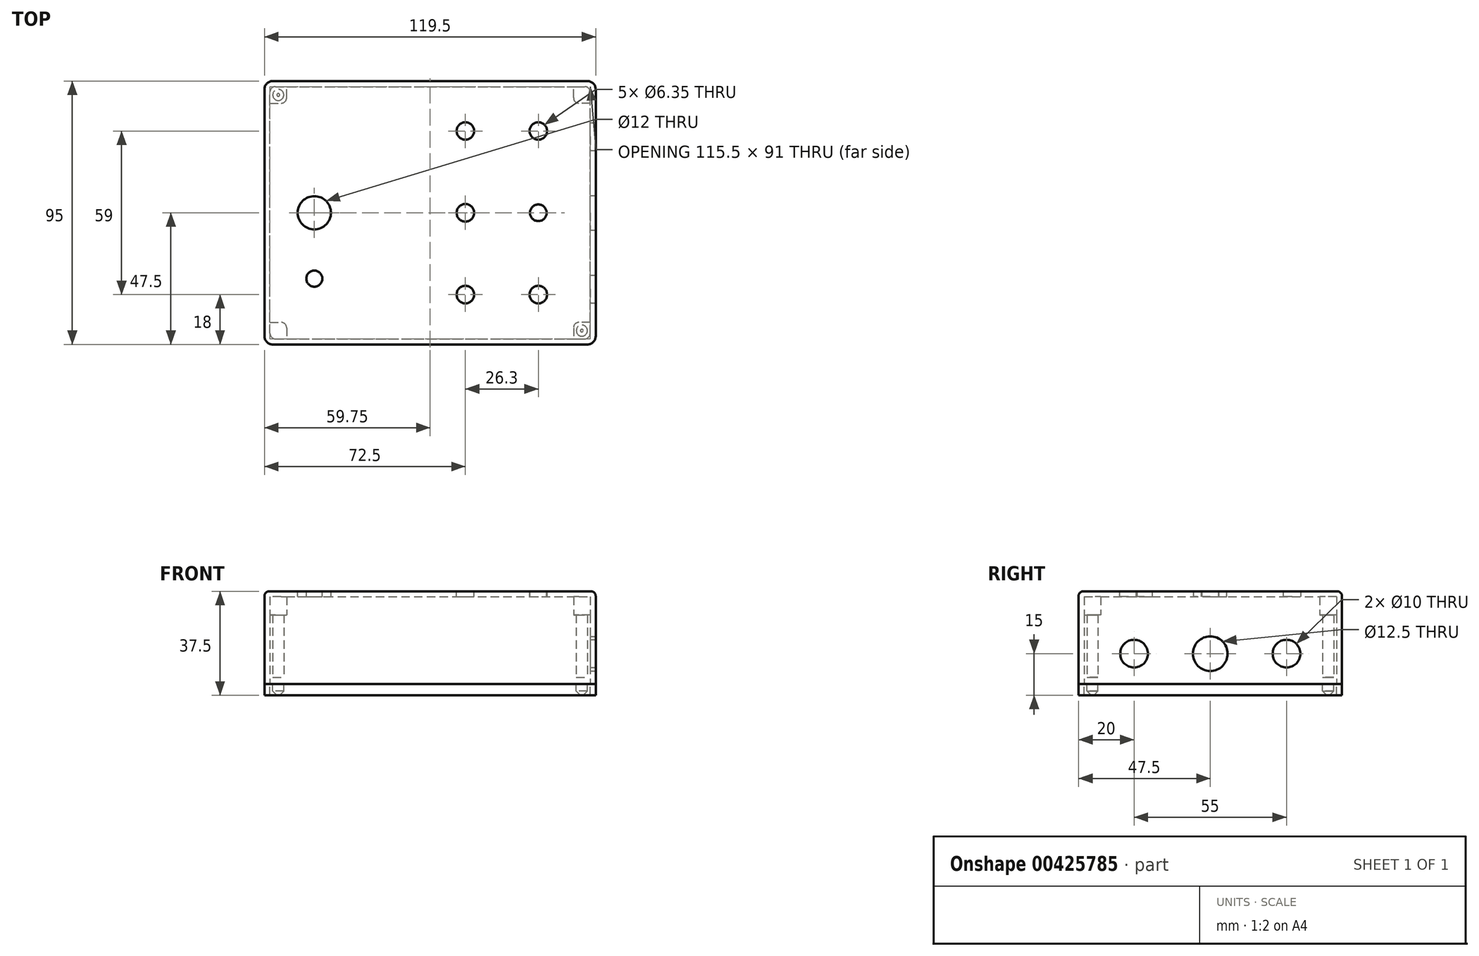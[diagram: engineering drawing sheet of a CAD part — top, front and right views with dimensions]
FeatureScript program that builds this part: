
annotation { "Feature Type Name" : "Feature", "Feature Type Description" : "" }
export const myFeature = defineFeature(function(context is Context, id is Id, definition is map)
    precondition{}
    {
        {
            var Q0;
            Q0=qCreatedBy(makeId("Top.planeOp"),FACE);
            var sketch = newSketch(context, id + "F0", { "sketchPlane" : qUnion([Q0])});
            skLineSegment(sketch, "E0.bottom", {"start": v(3, 0) * mm, "end": v(116.5, 0) * mm});
            skLineSegment(sketch, "E0.top", {"start": v(3, 95) * mm, "end": v(116.5, 95) * mm});
            skLineSegment(sketch, "E0.left", {"start": v(0, 3) * mm, "end": v(0, 92) * mm});
            skLineSegment(sketch, "E0.right", {"start": v(119.5, 3) * mm, "end": v(119.5, 92) * mm});
            skPoint(sketch, "E1.visualSharp", {"position": v(119.5, 95) * mm});
            skArc(sketch, "E1.filletArc", {"start": v(119.5, 92) * mm, "mid": v(118.62, 94.12) * mm, "end": v(116.5, 95) * mm});
            skPoint(sketch, "E2.visualSharp", {"position": v(119.5, 0) * mm});
            skArc(sketch, "E2.filletArc", {"start": v(116.5, 0) * mm, "mid": v(118.62, 0.88) * mm, "end": v(119.5, 3) * mm});
            skPoint(sketch, "E3.visualSharp", {"position": v(0, 0) * mm});
            skArc(sketch, "E3.filletArc", {"start": v(0, 3) * mm, "mid": v(0.88, 0.88) * mm, "end": v(3, 0) * mm});
            skPoint(sketch, "E4.visualSharp", {"position": v(0, 95) * mm});
            skArc(sketch, "E4.filletArc", {"start": v(3, 95) * mm, "mid": v(0.88, 94.12) * mm, "end": v(0, 92) * mm});
            skSolve(sketch);
        }
        {
            var Q0;
            Q0 = qSketchRegion(id + "F0", true);
            extrude(context, id + "F1", {"entities" : qUnion([Q0]), "depth" : 33.5 * mm});
        }
        {
            var Q0;
            Q0=makeQuery(id+"F1.opExtrude","CAP_FACE",FACE,{"disambiguationData":[OSD([sQuery(id+"F0.wireOp",EDGE,"E0.bottom"),sQuery(id+"F0.wireOp",EDGE,"E0.top"),sQuery(id+"F0.wireOp",EDGE,"E0.left"),sQuery(id+"F0.wireOp",EDGE,"E0.right"),sQuery(id+"F0.wireOp",EDGE,"E1.filletArc"),sQuery(id+"F0.wireOp",EDGE,"E2.filletArc"),sQuery(id+"F0.wireOp",EDGE,"E3.filletArc"),sQuery(id+"F0.wireOp",EDGE,"E4.filletArc")])],"isStart":true});
            var sketch = newSketch(context, id + "F2", { "sketchPlane" : qUnion([Q0])});
            skLineSegment(sketch, "E5.0", {"start": v(4.5, -2) * mm, "end": v(115, -2) * mm});
            skLineSegment(sketch, "E5.1", {"start": v(2, -4.5) * mm, "end": v(2, -90.5) * mm});
            skLineSegment(sketch, "E5.2", {"start": v(4.5, -93) * mm, "end": v(115, -93) * mm});
            skLineSegment(sketch, "E5.3", {"start": v(117.5, -4.5) * mm, "end": v(117.5, -90.5) * mm});
            skPoint(sketch, "E6.visualSharp", {"position": v(2, -2) * mm});
            skArc(sketch, "E6.filletArc", {"start": v(4.5, -2) * mm, "mid": v(2.73, -2.73) * mm, "end": v(2, -4.5) * mm});
            skPoint(sketch, "E7.visualSharp", {"position": v(117.5, -2) * mm});
            skArc(sketch, "E7.filletArc", {"start": v(117.5, -4.5) * mm, "mid": v(116.77, -2.73) * mm, "end": v(115, -2) * mm});
            skPoint(sketch, "E8.visualSharp", {"position": v(117.5, -93) * mm});
            skArc(sketch, "E8.filletArc", {"start": v(115, -93) * mm, "mid": v(116.77, -92.27) * mm, "end": v(117.5, -90.5) * mm});
            skPoint(sketch, "E9.visualSharp", {"position": v(2, -93) * mm});
            skArc(sketch, "E9.filletArc", {"start": v(2, -90.5) * mm, "mid": v(2.73, -92.27) * mm, "end": v(4.5, -93) * mm});
            skLineSegment(sketch, "E10", {"start": v(8, -2) * mm, "end": v(8, -6) * mm});
            skLineSegment(sketch, "E11", {"start": v(6, -8) * mm, "end": v(2, -8) * mm});
            skPoint(sketch, "E12.visualSharp", {"position": v(8, -8) * mm});
            skArc(sketch, "E12.filletArc", {"start": v(6, -8) * mm, "mid": v(7.41, -7.41) * mm, "end": v(8, -6) * mm});
            skLineSegment(sketch, "E13", {"start": v(59.75, 0) * mm, "end": v(59.75, -95) * mm, "construction": true});
            skLineSegment(sketch, "E14", {"start": v(0, -47.5) * mm, "end": v(119.5, -47.5) * mm, "construction": true});
            skLineSegment(sketch, "E15.MirrorCS", {"start": v(111.5, -2) * mm, "end": v(111.5, -6) * mm});
            skPoint(sketch, "E16.MirrorP", {"position": v(111.5, -8) * mm});
            skArc(sketch, "E17.MirrorCS", {"start": v(113.5, -8) * mm, "mid": v(112.09, -7.41) * mm, "end": v(111.5, -6) * mm});
            skLineSegment(sketch, "E18.MirrorCS", {"start": v(113.5, -8) * mm, "end": v(117.5, -8) * mm});
            skLineSegment(sketch, "E19.MirrorCS", {"start": v(6, -87) * mm, "end": v(2, -87) * mm});
            skArc(sketch, "E20.MirrorCS", {"start": v(6, -87) * mm, "mid": v(7.41, -87.59) * mm, "end": v(8, -89) * mm});
            skLineSegment(sketch, "E21.MirrorCS", {"start": v(8, -93) * mm, "end": v(8, -89) * mm});
            skLineSegment(sketch, "E22.MirrorCS", {"start": v(113.5, -87) * mm, "end": v(117.5, -87) * mm});
            skArc(sketch, "E23.MirrorCS", {"start": v(113.5, -87) * mm, "mid": v(112.09, -87.59) * mm, "end": v(111.5, -89) * mm});
            skLineSegment(sketch, "E24.MirrorCS", {"start": v(111.5, -93) * mm, "end": v(111.5, -89) * mm});
            skSolve(sketch);
        }
        {
            var Q0;
            {var subQ2=sQuery(id+"F2.wireOp",EDGE,"E10");Q0=makeQuery(id+"F2.imprint","IMPRINT",FACE,{"disambiguationData":[TD([[makeQuery(id+"F2.imprint","IMPRINT",EDGE,{"derivedFrom":subQ2}),1.0]])]});}
            extrude(context, id + "F3", {"entities" : qUnion([Q0]), "operationType" : NewBodyOperationType.REMOVE, "oppositeDirection" : true, "depth" : 31.5 * mm});
        }
        {
            var Q0;
            Q0=makeQuery(id+"F1.opExtrude","CAP_FACE",FACE,{"disambiguationData":[OSD([sQuery(id+"F0.wireOp",EDGE,"E0.bottom"),sQuery(id+"F0.wireOp",EDGE,"E0.top"),sQuery(id+"F0.wireOp",EDGE,"E0.left"),sQuery(id+"F0.wireOp",EDGE,"E0.right"),sQuery(id+"F0.wireOp",EDGE,"E1.filletArc"),sQuery(id+"F0.wireOp",EDGE,"E2.filletArc"),sQuery(id+"F0.wireOp",EDGE,"E3.filletArc"),sQuery(id+"F0.wireOp",EDGE,"E4.filletArc")])],"isStart":true});
            var sketch = newSketch(context, id + "F4", { "sketchPlane" : qUnion([Q0])});
            skLineSegment(sketch, "E25", {"start": v(8, -2) * mm, "end": v(4, -2) * mm});
            skLineSegment(sketch, "E26", {"start": v(2, -4) * mm, "end": v(2, -8) * mm});
            skLineSegment(sketch, "E27", {"start": v(111.5, -2) * mm, "end": v(115.5, -2) * mm});
            skLineSegment(sketch, "E28", {"start": v(117.5, -4) * mm, "end": v(117.5, -8) * mm});
            skLineSegment(sketch, "E29", {"start": v(117.5, -87) * mm, "end": v(117.5, -91) * mm});
            skLineSegment(sketch, "E30", {"start": v(115.5, -93) * mm, "end": v(111.5, -93) * mm});
            skLineSegment(sketch, "E31", {"start": v(8, -93) * mm, "end": v(4, -93) * mm});
            skLineSegment(sketch, "E32", {"start": v(2, -91) * mm, "end": v(2, -87) * mm});
            skPoint(sketch, "E33.visualSharp", {"position": v(2, -2) * mm});
            skArc(sketch, "E33.filletArc", {"start": v(4, -2) * mm, "mid": v(2.59, -2.59) * mm, "end": v(2, -4) * mm});
            skPoint(sketch, "E34.visualSharp", {"position": v(117.5, -2) * mm});
            skArc(sketch, "E34.filletArc", {"start": v(117.5, -4) * mm, "mid": v(116.91, -2.59) * mm, "end": v(115.5, -2) * mm});
            skPoint(sketch, "E35.visualSharp", {"position": v(117.5, -93) * mm});
            skArc(sketch, "E35.filletArc", {"start": v(115.5, -93) * mm, "mid": v(116.91, -92.41) * mm, "end": v(117.5, -91) * mm});
            skPoint(sketch, "E36.visualSharp", {"position": v(2, -93) * mm});
            skArc(sketch, "E36.filletArc", {"start": v(2, -91) * mm, "mid": v(2.59, -92.41) * mm, "end": v(4, -93) * mm});
            skSolve(sketch);
        }
        {
            var Q0;
            Q0=makeQuery(id+"F4.imprint","IMPRINT",FACE,{"disambiguationData":[TD([[makeQuery(id+"F4.imprint","IMPRINT",EDGE,{"derivedFrom":sQuery(id+"F4.wireOp",EDGE,"E25")}),1.0]])]});
            var Q1;
            Q1=makeQuery(id+"F4.imprint","IMPRINT",FACE,{"disambiguationData":[TD([[makeQuery(id+"F4.imprint","IMPRINT",EDGE,{"derivedFrom":sQuery(id+"F4.wireOp",EDGE,"E27")}),-1.0]])]});
            var Q2;
            Q2=makeQuery(id+"F4.imprint","IMPRINT",FACE,{"disambiguationData":[TD([[makeQuery(id+"F4.imprint","IMPRINT",EDGE,{"derivedFrom":sQuery(id+"F4.wireOp",EDGE,"E29")}),-1.0]])]});
            var Q3;
            Q3=makeQuery(id+"F4.imprint","IMPRINT",FACE,{"disambiguationData":[TD([[makeQuery(id+"F4.imprint","IMPRINT",EDGE,{"derivedFrom":sQuery(id+"F4.wireOp",EDGE,"E31")}),-1.0]])]});
            extrude(context, id + "F5", {"entities" : qUnion([Q0, Q1, Q2, Q3]), "operationType" : NewBodyOperationType.REMOVE, "oppositeDirection" : true, "depth" : 2.5 * mm});
        }
        {
            var Q0;
            Q0=makeQuery(id+"F1.opExtrude","CAP_FACE",FACE,{"disambiguationData":[OSD([sQuery(id+"F0.wireOp",EDGE,"E0.bottom"),sQuery(id+"F0.wireOp",EDGE,"E0.top"),sQuery(id+"F0.wireOp",EDGE,"E0.left"),sQuery(id+"F0.wireOp",EDGE,"E0.right"),sQuery(id+"F0.wireOp",EDGE,"E1.filletArc"),sQuery(id+"F0.wireOp",EDGE,"E2.filletArc"),sQuery(id+"F0.wireOp",EDGE,"E3.filletArc"),sQuery(id+"F0.wireOp",EDGE,"E4.filletArc")])],"isStart":true});
            var sketch = newSketch(context, id + "F6", { "sketchPlane" : qUnion([Q0])});
            skCircle(sketch, "E37", {"center": v(5, -5) * mm, "radius": 2 * mm});
            skLineSegment(sketch, "E38", {"start": v(59.75, 0) * mm, "end": v(59.75, -95) * mm, "construction": true});
            skLineSegment(sketch, "E39", {"start": v(119.5, -47.5) * mm, "end": v(0, -47.5) * mm, "construction": true});
            skCircle(sketch, "E40.MirrorC", {"center": v(114.5, -5) * mm, "radius": 2 * mm});
            skLineSegment(sketch, "E41.MirrorCS", {"start": v(0, -47.5) * mm, "end": v(119.5, -47.5) * mm, "construction": true});
            skCircle(sketch, "E42.MirrorC", {"center": v(5, -90) * mm, "radius": 2 * mm});
            skCircle(sketch, "E43.MirrorC", {"center": v(114.5, -90) * mm, "radius": 2 * mm});
            skSolve(sketch);
        }
        {
            var Q0;
            Q0=makeQuery(id+"F6.imprint","IMPRINT",FACE,{"disambiguationData":[TD([[makeQuery(id+"F6.imprint","IMPRINT",EDGE,{"derivedFrom":sQuery(id+"F6.wireOp",EDGE,"E37")}),1.0]])]});
            var Q1;
            Q1=makeQuery(id+"F6.imprint","IMPRINT",FACE,{"disambiguationData":[TD([[makeQuery(id+"F6.imprint","IMPRINT",EDGE,{"derivedFrom":sQuery(id+"F6.wireOp",EDGE,"E40.MirrorC")}),-1.0]])]});
            var Q2;
            Q2=makeQuery(id+"F6.imprint","IMPRINT",FACE,{"disambiguationData":[TD([[makeQuery(id+"F6.imprint","IMPRINT",EDGE,{"derivedFrom":sQuery(id+"F6.wireOp",EDGE,"E43.MirrorC")}),1.0]])]});
            var Q3;
            Q3=makeQuery(id+"F6.imprint","IMPRINT",FACE,{"disambiguationData":[TD([[makeQuery(id+"F6.imprint","IMPRINT",EDGE,{"derivedFrom":sQuery(id+"F6.wireOp",EDGE,"E42.MirrorC")}),-1.0]])]});
            extrude(context, id + "F7", {"entities" : qUnion([Q0, Q1, Q2, Q3]), "operationType" : NewBodyOperationType.REMOVE, "oppositeDirection" : true, "depth" : 25 * mm});
        }
        {
            var Q0;
            Q0 = qSketchRegion(id + "F0", true);
            extrude(context, id + "F8", {"entities" : qUnion([Q0]), "oppositeDirection" : true, "depth" : 4 * mm});
        }
        {
            var Q0;
            Q0=makeQuery(id+"F6.imprint","IMPRINT",FACE,{"disambiguationData":[TD([[makeQuery(id+"F6.imprint","IMPRINT",EDGE,{"derivedFrom":sQuery(id+"F6.wireOp",EDGE,"E37")}),1.0]])]});
            var Q1;
            Q1=makeQuery(id+"F6.imprint","IMPRINT",FACE,{"disambiguationData":[TD([[makeQuery(id+"F6.imprint","IMPRINT",EDGE,{"derivedFrom":sQuery(id+"F6.wireOp",EDGE,"E40.MirrorC")}),-1.0]])]});
            var Q2;
            Q2=makeQuery(id+"F6.imprint","IMPRINT",FACE,{"disambiguationData":[TD([[makeQuery(id+"F6.imprint","IMPRINT",EDGE,{"derivedFrom":sQuery(id+"F6.wireOp",EDGE,"E43.MirrorC")}),1.0]])]});
            var Q3;
            Q3=makeQuery(id+"F6.imprint","IMPRINT",FACE,{"disambiguationData":[TD([[makeQuery(id+"F6.imprint","IMPRINT",EDGE,{"derivedFrom":sQuery(id+"F6.wireOp",EDGE,"E42.MirrorC")}),-1.0]])]});
            extrude(context, id + "F9", {"entities" : qUnion([Q0, Q1, Q2, Q3]), "operationType" : NewBodyOperationType.REMOVE, "endBound" : BoundingType.THROUGH_ALL, "depth" : 25 * mm});
        }
        {
            var Q0;
            Q0=makeQuery(id+"F9.boolean.opBoolean","INTERSECT",EDGE,{"derivedFrom":[makeQuery(id+"F8.opExtrude","CAP_FACE",FACE,{"disambiguationData":[OSD([sQuery(id+"F0.wireOp",EDGE,"E0.bottom"),sQuery(id+"F0.wireOp",EDGE,"E0.top"),sQuery(id+"F0.wireOp",EDGE,"E0.left"),sQuery(id+"F0.wireOp",EDGE,"E0.right"),sQuery(id+"F0.wireOp",EDGE,"E1.filletArc"),sQuery(id+"F0.wireOp",EDGE,"E2.filletArc"),sQuery(id+"F0.wireOp",EDGE,"E3.filletArc"),sQuery(id+"F0.wireOp",EDGE,"E4.filletArc")])],"isStart":false}),makeQuery(id+"F9.opExtrude","SWEPT_FACE",FACE,{"disambiguationData":[OSD([sQuery(id+"F6.wireOp",EDGE,"E37")])]})]});
            var Q1;
            Q1=makeQuery(id+"F9.boolean.opBoolean","INTERSECT",EDGE,{"derivedFrom":[makeQuery(id+"F8.opExtrude","CAP_FACE",FACE,{"disambiguationData":[OSD([sQuery(id+"F0.wireOp",EDGE,"E0.bottom"),sQuery(id+"F0.wireOp",EDGE,"E0.top"),sQuery(id+"F0.wireOp",EDGE,"E0.left"),sQuery(id+"F0.wireOp",EDGE,"E0.right"),sQuery(id+"F0.wireOp",EDGE,"E1.filletArc"),sQuery(id+"F0.wireOp",EDGE,"E2.filletArc"),sQuery(id+"F0.wireOp",EDGE,"E3.filletArc"),sQuery(id+"F0.wireOp",EDGE,"E4.filletArc")])],"isStart":false}),makeQuery(id+"F9.opExtrude","SWEPT_FACE",FACE,{"disambiguationData":[OSD([sQuery(id+"F6.wireOp",EDGE,"E40.MirrorC")])]})]});
            var Q2;
            Q2=makeQuery(id+"F9.boolean.opBoolean","INTERSECT",EDGE,{"derivedFrom":[makeQuery(id+"F8.opExtrude","CAP_FACE",FACE,{"disambiguationData":[OSD([sQuery(id+"F0.wireOp",EDGE,"E0.bottom"),sQuery(id+"F0.wireOp",EDGE,"E0.top"),sQuery(id+"F0.wireOp",EDGE,"E0.left"),sQuery(id+"F0.wireOp",EDGE,"E0.right"),sQuery(id+"F0.wireOp",EDGE,"E1.filletArc"),sQuery(id+"F0.wireOp",EDGE,"E2.filletArc"),sQuery(id+"F0.wireOp",EDGE,"E3.filletArc"),sQuery(id+"F0.wireOp",EDGE,"E4.filletArc")])],"isStart":false}),makeQuery(id+"F9.opExtrude","SWEPT_FACE",FACE,{"disambiguationData":[OSD([sQuery(id+"F6.wireOp",EDGE,"E43.MirrorC")])]})]});
            var Q3;
            Q3=makeQuery(id+"F9.boolean.opBoolean","INTERSECT",EDGE,{"derivedFrom":[makeQuery(id+"F8.opExtrude","CAP_FACE",FACE,{"disambiguationData":[OSD([sQuery(id+"F0.wireOp",EDGE,"E0.bottom"),sQuery(id+"F0.wireOp",EDGE,"E0.top"),sQuery(id+"F0.wireOp",EDGE,"E0.left"),sQuery(id+"F0.wireOp",EDGE,"E0.right"),sQuery(id+"F0.wireOp",EDGE,"E1.filletArc"),sQuery(id+"F0.wireOp",EDGE,"E2.filletArc"),sQuery(id+"F0.wireOp",EDGE,"E3.filletArc"),sQuery(id+"F0.wireOp",EDGE,"E4.filletArc")])],"isStart":false}),makeQuery(id+"F9.opExtrude","SWEPT_FACE",FACE,{"disambiguationData":[OSD([sQuery(id+"F6.wireOp",EDGE,"E42.MirrorC")])]})]});
            chamfer(context, id + "F10", {"entities" : qUnion([Q0, Q1, Q2, Q3]), "width" : 1.5 * mm, "tangentPropagation" : true});
        }
        {
            var Q0;
            Q0=makeQuery(id+"F8.opExtrude","CAP_FACE",FACE,{"disambiguationData":[OSD([sQuery(id+"F0.wireOp",EDGE,"E0.bottom"),sQuery(id+"F0.wireOp",EDGE,"E0.top"),sQuery(id+"F0.wireOp",EDGE,"E0.left"),sQuery(id+"F0.wireOp",EDGE,"E0.right"),sQuery(id+"F0.wireOp",EDGE,"E1.filletArc"),sQuery(id+"F0.wireOp",EDGE,"E2.filletArc"),sQuery(id+"F0.wireOp",EDGE,"E3.filletArc"),sQuery(id+"F0.wireOp",EDGE,"E4.filletArc")])],"isStart":false});
            var Q1;
            Q1=makeQuery(id+"F1.opExtrude","CAP_FACE",FACE,{"disambiguationData":[OSD([sQuery(id+"F0.wireOp",EDGE,"E0.bottom"),sQuery(id+"F0.wireOp",EDGE,"E0.top"),sQuery(id+"F0.wireOp",EDGE,"E0.left"),sQuery(id+"F0.wireOp",EDGE,"E0.right"),sQuery(id+"F0.wireOp",EDGE,"E1.filletArc"),sQuery(id+"F0.wireOp",EDGE,"E2.filletArc"),sQuery(id+"F0.wireOp",EDGE,"E3.filletArc"),sQuery(id+"F0.wireOp",EDGE,"E4.filletArc")])],"isStart":false});
            fillet(context, id + "F11", {"entities" : qUnion([Q0, Q1]), "radius" : 1.7 * mm, "tangentPropagation" : true, "allowEdgeOverflow" : false});
        }
        {
            var Q0;
            Q0=makeQuery(id+"F1.opExtrude","CAP_FACE",FACE,{"disambiguationData":[OSD([sQuery(id+"F0.wireOp",EDGE,"E0.bottom"),sQuery(id+"F0.wireOp",EDGE,"E0.top"),sQuery(id+"F0.wireOp",EDGE,"E0.left"),sQuery(id+"F0.wireOp",EDGE,"E0.right"),sQuery(id+"F0.wireOp",EDGE,"E1.filletArc"),sQuery(id+"F0.wireOp",EDGE,"E2.filletArc"),sQuery(id+"F0.wireOp",EDGE,"E3.filletArc"),sQuery(id+"F0.wireOp",EDGE,"E4.filletArc")])],"isStart":false});
            var sketch = newSketch(context, id + "F12", { "sketchPlane" : qUnion([Q0])});
            skCircle(sketch, "E44", {"center": v(72.5, 77) * mm, "radius": 3.17 * mm});
            skLineSegment(sketch, "E45", {"start": v(1.7, 47.5) * mm, "end": v(117.8, 47.5) * mm, "construction": true});
            skCircle(sketch, "E46.MirrorC", {"center": v(72.5, 18) * mm, "radius": 3.17 * mm});
            skCircle(sketch, "E47", {"center": v(72.5, 47.5) * mm, "radius": 3.17 * mm});
            skCircle(sketch, "E48", {"center": v(98.8, 77) * mm, "radius": 3.17 * mm});
            skCircle(sketch, "E49.MirrorC", {"center": v(98.8, 18) * mm, "radius": 3.17 * mm});
            skCircle(sketch, "E50", {"center": v(98.8, 47.5) * mm, "radius": 3 * mm});
            skCircle(sketch, "E51", {"center": v(18, 47.5) * mm, "radius": 6 * mm});
            skCircle(sketch, "E52", {"center": v(18, 23.75) * mm, "radius": 2.9 * mm});
            skSolve(sketch);
        }
        {
            var Q0;
            Q0 = qSketchRegion(id + "F12", true);
            extrude(context, id + "F13", {"entities" : qUnion([Q0]), "operationType" : NewBodyOperationType.REMOVE, "endBound" : BoundingType.UP_TO_NEXT, "oppositeDirection" : true, "depth" : 25 * mm});
        }
        {
            var Q0;
            Q0=makeQuery(id+"F1.opExtrude","SWEPT_FACE",FACE,{"disambiguationData":[OSD([sQuery(id+"F0.wireOp",EDGE,"E0.right")])]});
            var sketch = newSketch(context, id + "F14", { "sketchPlane" : qUnion([Q0])});
            skLineSegment(sketch, "E53", {"start": v(-12.27, 11) * mm, "end": v(115.43, 11) * mm, "construction": true});
            skLineSegment(sketch, "E54.0", {"start": v(3, 33.5) * mm, "end": v(92, 33.5) * mm, "construction": true});
            skLineSegment(sketch, "E55.0", {"start": v(87.4, -4) * mm, "end": v(7.6, -4) * mm, "construction": true});
            skCircle(sketch, "E56", {"center": v(20, 11) * mm, "radius": 5 * mm});
            skCircle(sketch, "E57", {"center": v(75, 11) * mm, "radius": 5 * mm});
            skCircle(sketch, "E58", {"center": v(47.5, 11) * mm, "radius": 6.25 * mm});
            skSolve(sketch);
        }
        {
            var Q0;
            Q0 = qSketchRegion(id + "F14", true);
            extrude(context, id + "F15", {"entities" : qUnion([Q0]), "operationType" : NewBodyOperationType.REMOVE, "oppositeDirection" : true, "depth" : 25 * mm});
        }
    });
